# Revit family: Mini_System-Carnes-Energy_Recovery-WMA-WMWA-ARR6
name_source: partatom
category: Mechanical Equipment
revit_build: Autodesk Revit Architecture 2012 (Build: 20110309_2315(x64)
units: mm (PartAtom-declared; Revit-internal decimal feet)

## types (8) — shared parameters
Description = Energy Recovery Mini System
Duct Arrangement = 1
Eliminator = <By Category>
Exhaust Hood Height = 17"
Exhaust Hood Width = 12 1/4"
Exhaust Location From End = 4"
Exhuast Hood Depth = 14 1/4"
Handle = Plastic - Carnes - Smooth - Black
Manufacturer = CARNES COMPANY
Model = WM_A-ARR6
Product Page URL = http://www.carnes.com
Supply Location From End = 4"
Supply Location From Side = 4"
URL = http://www.carnes.com
Unit = Metal - Carnes - Aluminum Frame - Painted White
Weight = 0.00 lb

## per-type parameters (varying)
| type | Exhaust Height | Exhaust Location From Bottom | Exhaust Width | Height of Unit | Intake Height | Intake Location From Bottom | Intake Width | Length of Unit | Return Height | Return Location From Bottom | Return Width | Service Clearance Exhaust Side | Service Clearance Supply Side | Size | Supply Height | Supply Location From Bottom | Supply Width | Width of Unit |
| Size 3, Standard | 14" | 6 1/2" | 16" | 44" | 21" | 19" | 16" | 60" | 16" | 6 1/2" | 14" | 50" | 50" | 3 | 14" | 6 1/2" | 16" | 47 1/2" |
| Size 3, Water Coils | 14" | 6 1/2" | 16" | 44" | 21" | 19" | 16" | 108" | 16" | 6 1/2" | 14" | 50" | 50" | 3 | 14" | 6 1/2" | 16" | 47 1/2" |
| Size 3, Rain Hood | 18" | 6 1/2" | 20" | 54" | 26" | 24" | 22" | 72" | 20" | 6 1/2" | 18" | 60" | 60" | 6 | 18" | 6 1/2" | 20" | 57 1/2" |
| Size 3, Rain Hood w/ Water Coils | 18" | 6 1/2" | 20" | 54" | 26" | 24" | 22" | 120" | 20" | 6 1/2" | 18" | 60" | 60" | 6 | 18" | 6 1/2" | 20" | 57 1/2" |
| Size 6, Standard | 20" | 7 1/2" | 24" | 66" | 34" | 28" | 28" | 80" | 24" | 7 1/2" | 20" | 71" | 71" | 9 | 20" | 7 1/2" | 24" | 69 1/2" |
| Size 6, Water Coils | 20" | 7 1/2" | 24" | 66" | 34" | 28" | 28" | 128" | 24" | 7 1/2" | 20" | 71" | 71" | 9 | 20" | 7 1/2" | 24" | 69 1/2" |
| Size 6, Rain Hood | 24" | 9 1/2" | 30" | 80" | 42" | 34" | 34" | 102" | 30" | 9 1/2" | 24" | 85" | 85" | 14 | 24" | 9 1/2" | 30" | 83 1/2" |
| Size 6, Rain Hood w/ Water Coils | 24" | 9 1/2" | 30" | 80" | 42" | 34" | 34" | 150" | 30" | 9 1/2" | 24" | 85" | 85" | 14 | 24" | 9 1/2" | 30" | 83 1/2" |

## geometry (parser evidence)
native form markers: Blend x6, Sweep x7
no freeform markers — native parametric forms only
